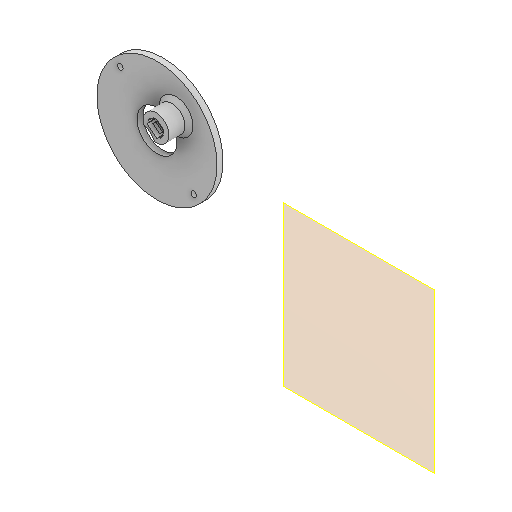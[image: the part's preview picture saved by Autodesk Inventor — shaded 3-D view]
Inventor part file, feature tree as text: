
AUTODESK INVENTOR PART (.ipt)
format: ipt  version: 2022 (Build 260153000, 153)  size: 217,088 bytes
history: native  units: in
note: dims shown in document units (in); Inventor stores cm internally (conversion verified against a paired STEP export)
features: reference x24, other x8, extrude x6, sketch x5, projected_geometry x3, plane x1, chamfer x1
ambient origin geometry x8: Origin, YZ Plane, XZ Plane, XY Plane, X Axis, Y Axis, Z Axis, Center Point
bodies: Volumenkörper1 (feature_tree)
feature tree (48):
  other  "00_toslink_launcher_v3.ipt"
  plane  "Arbeitsebene1"
  extrude  "Extrusion1"  Depth=0.1181in TaperAngle=0.0deg
  extrude  "Extrusion4"  Depth=0.3937in
  extrude  "Extrusion5"  Depth=0.3937in TaperAngle=0.0deg
  extrude  "Extrusion6"  Depth=2.3622in
  extrude  "Extrusion7"  Depth=0.0394in TaperAngle=0.0deg
  chamfer  "Chamfer1"  Distance=0.0787in Angle=45.0deg
  extrude  "Extrusion8"  TaperAngle=45.0deg  [1 undecoded]
  reference  "Referenz1"
  reference  "Reference2"
  reference  "Reference3"
  sketch  "Sketch4"  dims[d0=0.7874in d1=0.1181in d2=0.0in]
  reference  "Reference4"
  sketch  "Sketch6"  dims[d13=0.3937in d14=0.0in d16=0.3937in]
  reference  "Reference7"
  reference  "Reference8"
  reference  "Reference9"
  reference  "Reference10"
  reference  "Reference11"
  reference  "Reference12"
  reference  "Reference13"
  reference  "Reference14"
  reference  "Reference15"
  projected_geometry  "Projected Loop5"
  reference  "Reference16"
  reference  "Reference17"
  reference  "Reference18"
  reference  "Reference19"
  reference  "Reference20"
  reference  "Reference21"
  reference  "Reference22"
  reference  "Reference23"
  reference  "Reference24"
  reference  "Reference25"
  sketch  "Sketch7"  dims[d17=0.5118in d18=0.3937in d19=0.0in]
  sketch  "Sketch8"  dims[d20=0.2362in d21=2.3622in]
  projected_geometry  "Projected Loop6"
  sketch  "Sketch9"  dims[d22=0.0394in d23=0.0in d24=0.0394in d25=0.0in d26=0.0787in d27=0.0787in d28=45.0deg d29=45.0deg d30=0.0in d31=0.1102in d32=0.1102in d33=0.0in d34=0.0in]
  reference  "Reference26"
  projected_geometry  "Projected Loop7"
  other  "Anglerfish_bonne_mamman_v0.iam"
  other  "00_bonne_maman_jar:1"
  other  "00_ESP3-CAM:1"
  other  "Bauteil50"
  other  "00_toslink_launcher_v3:1"
  other  "Matchboxscope_M12_Lensadapter_v0:1"
  other  "Anglerfish_Jar_Adapterplate_v1:1"
note: 1 required parameter value undecoded (feature->parameter linkage not recoverable at this tier; creation-order binding heuristic only, values carry confidence <= 0.55)
